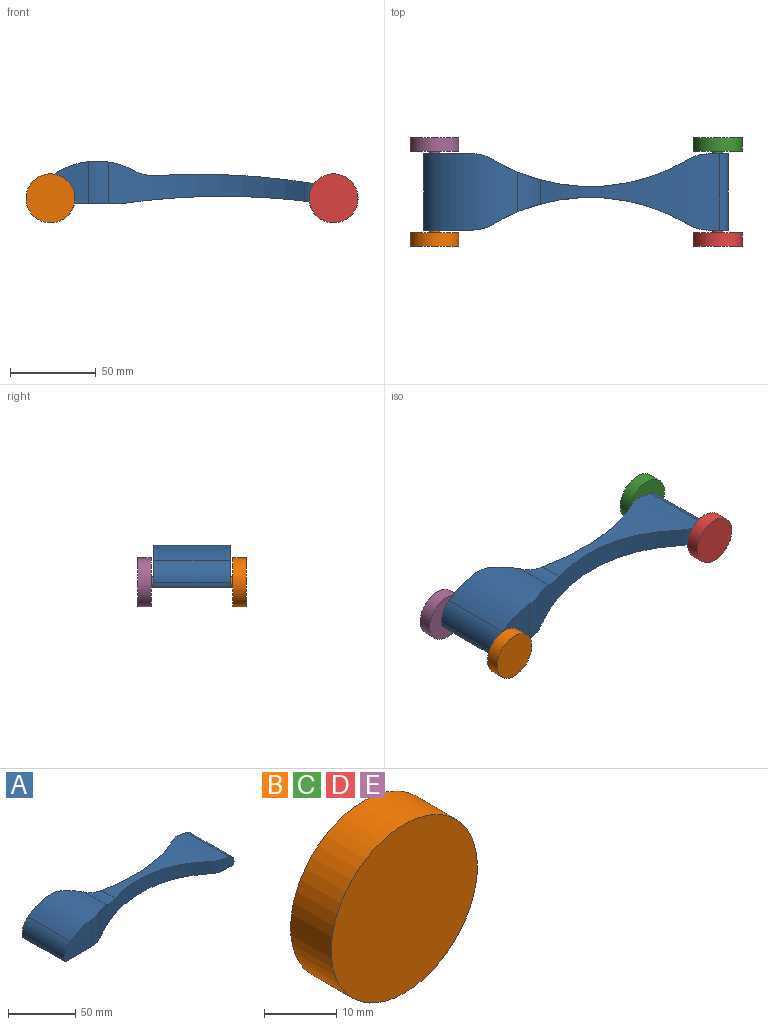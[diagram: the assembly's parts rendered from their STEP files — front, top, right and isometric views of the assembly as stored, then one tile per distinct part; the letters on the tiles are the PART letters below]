
ASSEMBLY  parts=5 mates=4
PART A: 23 faces, bbox 177.8x44.5x24.9 mm
  f0: plane 46.77x44.45mm, normal (0,0,-1), area 834.5mm2, adj f1,f2,f6,f12,f16,f18,f19,f20
  f1: plane 28.58x24.62mm, normal (0,1,0), area 551.1mm2, adj f0,f3,f11,f15,f16,f19
  f2: plane 28.58x24.62mm, normal (0,-1,0), area 551.1mm2, adj f0,f3,f11,f15,f16,f22
  f3: cylinder r=44.98mm len=48.38mm, axis (0,-1,0), area 2030.1mm2, adj f1,f2,f4,f15,f18,f19,f20,f22
  f4: cylinder r=25.4mm len=23.27mm, axis (0,-1,0), area 260.4mm2, adj f3,f5,f18,f20
  f5: cylinder r=406.4mm len=104.32mm, axis (0,-1,0), area 2010.3mm2, adj f4,f8,f9,f14,f17,f18,f20,f21
  f6: cylinder r=406.4mm len=118.33mm, axis (0,-1,0), area 2141.3mm2, adj f0,f7,f17,f18,f20,f21
  f7: plane 44.45x11mm, normal (0,0,-1), area 488.9mm2, adj f6,f8,f9,f14
  f8: plane 11.85x10.69mm, normal (0,1,0), area 106.6mm2, adj f5,f7,f10,f14,f17
  f9: plane 11.85x10.69mm, normal (0,-1,0), area 106.6mm2, adj f5,f7,f10,f14,f21
  f10: cylinder r=0.32mm len=44.45mm, axis (0,-1,0), area 89.7mm2, adj f8,f9
  f11: cylinder r=0.32mm len=44.45mm, axis (0,-1,0), area 89.7mm2, adj f1,f2
  f12: cylinder r=19.05mm len=38.1mm, axis (0,0,-1), area 1520.1mm2, adj f0,f13
  f13: plane 38.1x38.1mm, normal (0,0,-1), area 1140.1mm2, adj f12
  f14: cylinder r=6.35mm len=44.45mm, axis (0,-1,0), area 535.7mm2, adj f5,f7,f8,f9
  f15: cylinder r=15.88mm len=44.45mm, axis (0,-1,0), area 654.3mm2, adj f1,f2,f3,f16
  f16: cylinder r=6.35mm len=44.45mm, axis (0,-1,0), area 147.8mm2, adj f0,f1,f2,f15
  f17: cylinder r=22.23mm len=12.59mm, axis (0,0,-1), area 130.9mm2, adj f5,f6,f8,f18
  f18: cylinder r=111.13mm len=114.48mm, axis (0,0,-1), area 1705.1mm2, adj f0,f3,f4,f5,f6,f17,f19
  f19: cylinder r=22.23mm len=24.87mm, axis (0,0,-1), area 297.4mm2, adj f0,f1,f3,f18
  f20: cylinder r=111.13mm len=114.48mm, axis (0,0,-1), area 1705.1mm2, adj f0,f3,f4,f5,f6,f21,f22
  f21: cylinder r=22.23mm len=12.59mm, axis (0,0,-1), area 130.9mm2, adj f5,f6,f9,f20
  f22: cylinder r=22.23mm len=24.87mm, axis (0,0,-1), area 297.4mm2, adj f0,f2,f3,f20
PART B: 5 faces, bbox 28.6x9.5x28.6 mm
  f0: cylinder r=14.29mm len=28.58mm, axis (0,1,0), area 712.6mm2, adj f1,f2
  f1: plane 28.58x28.58mm, normal (0,-1,0), area 641.3mm2, adj f0
  f2: plane 28.58x28.58mm, normal (0,1,0), area 609.6mm2, adj f0,f3
  f3: cylinder r=3.17mm len=6.35mm, axis (0,-1,0), area 31.7mm2, adj f2,f4
  f4: plane 6.35x6.35mm, normal (0,1,0), area 31.7mm2, adj f3
PART C: same geometry as B
PART D: same geometry as B
PART E: same geometry as B
PLACE A at identity fixed
PLACE B t=(-82.55,-23.81,3.17)mm
PLACE C rot(axis=(1,0,0),180deg) t=(82.55,23.81,3.18)mm
PLACE D t=(82.55,-23.81,3.18)mm
PLACE E rot(axis=(1,0,0),180deg) t=(-82.55,23.81,3.18)mm
MATE fastened E.f3 <-> A.f11  axis (0,-1,0) through (-82.55,22.23,3.18)mm
MATE fastened C.f3 <-> A.f10  axis (0,-1,0) through (82.55,22.22,3.18)mm
MATE fastened D.f3 <-> A.f10  axis (0,1,0) through (82.55,-22.23,3.18)mm
MATE fastened B.f3 <-> A.f11  axis (0,1,0) through (-82.55,-22.22,3.17)mm
